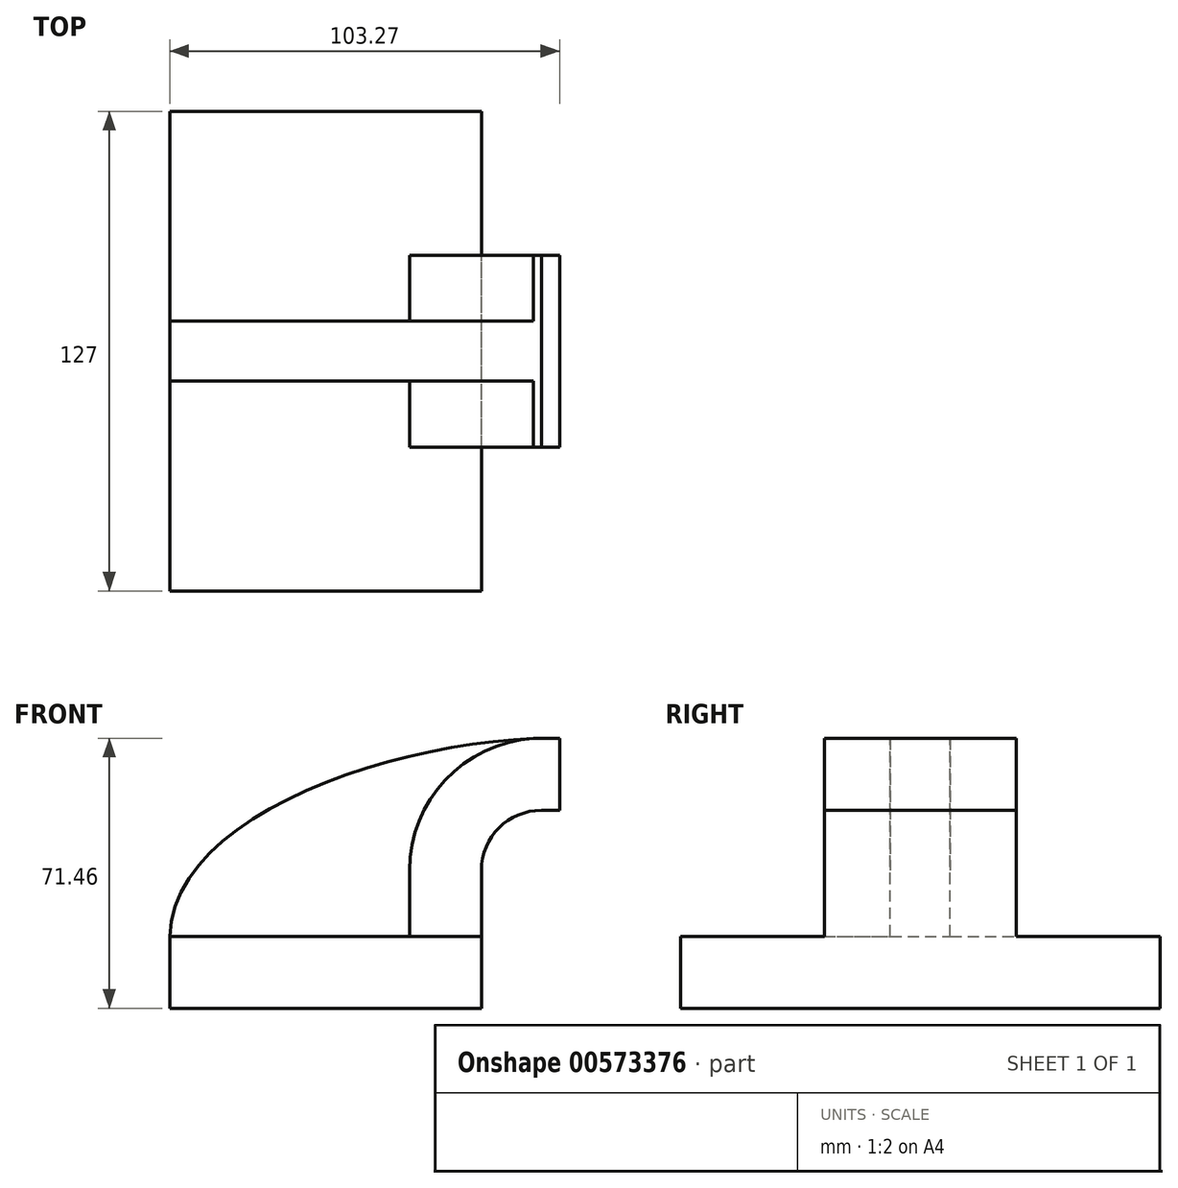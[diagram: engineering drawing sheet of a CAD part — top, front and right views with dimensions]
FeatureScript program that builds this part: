
annotation { "Feature Type Name" : "Feature", "Feature Type Description" : "" }
export const myFeature = defineFeature(function(context is Context, id is Id, definition is map)
    precondition{}
    {
        {
            var Q0;
            Q0=qCreatedBy(makeId("Front.planeOp"),FACE);
            var sketch = newSketch(context, id + "F0", { "sketchPlane" : qUnion([Q0])});
            skLineSegment(sketch, "E0.bottom", {"start": v(-41.28, -9.53) * mm, "end": v(41.28, -9.53) * mm});
            skLineSegment(sketch, "E0.top", {"start": v(-41.28, 9.53) * mm, "end": v(41.28, 9.53) * mm});
            skLineSegment(sketch, "E0.left", {"start": v(-41.28, -9.53) * mm, "end": v(-41.28, 9.53) * mm});
            skLineSegment(sketch, "E0.right", {"start": v(41.28, -9.53) * mm, "end": v(41.28, 9.53) * mm});
            skPoint(sketch, "E0.middle", {"position": v(0, 0) * mm});
            skLineSegment(sketch, "E1.bottom", {"start": v(109.46, 38.1) * mm, "end": v(62, 38.1) * mm});
            skLineSegment(sketch, "E1.top", {"start": v(109.46, 66.67) * mm, "end": v(62, 66.67) * mm});
            skLineSegment(sketch, "E1.left", {"start": v(109.46, 38.1) * mm, "end": v(109.46, 66.67) * mm});
            skLineSegment(sketch, "E1.right", {"start": v(62, 38.1) * mm, "end": v(62, 66.67) * mm});
            skPoint(sketch, "E1.middle", {"position": v(85.72, 52.39) * mm});
            skLineSegment(sketch, "E2", {"start": v(41.27, 9.53) * mm, "end": v(41.27, 27) * mm});
            skArc(sketch, "E3", {"start": v(41.27, 27) * mm, "mid": v(45.92, 38.23) * mm, "end": v(57.15, 42.88) * mm});
            skLineSegment(sketch, "E4", {"start": v(57.15, 42.88) * mm, "end": v(83.61, 42.88) * mm});
            skLineSegment(sketch, "E5.0", {"start": v(57.15, 61.93) * mm, "end": v(83.61, 61.93) * mm});
            skArc(sketch, "E5.1", {"start": v(22.23, 27) * mm, "mid": v(32.45, 51.7) * mm, "end": v(57.15, 61.93) * mm});
            skLineSegment(sketch, "E5.2", {"start": v(22.22, 9.53) * mm, "end": v(22.22, 27) * mm});
            skFitSpline(sketch, "E6", {"points": [v(-41.28, 9.53) * mm, v(57.15, 61.93) * mm], "startDerivative": vector(2.5, 96.11) * mm, "endDerivative": vector(118.65, 2.68) * mm});
            skLineSegment(sketch, "E7", {"start": v(83.61, 61.93) * mm, "end": v(83.61, 42.88) * mm});
            skSolve(sketch);
        }
        {
            var Q0;
            Q0=makeQuery(id+"F0.imprint","IMPRINT",FACE,{"disambiguationData":[TD([[makeQuery(id+"F0.imprint","IMPRINT",EDGE,{"derivedFrom":sQuery(id+"F0.wireOp",EDGE,"E0.bottom")}),1.0]])]});
            extrude(context, id + "F1", {"entities" : qUnion([Q0]), "endBound" : BoundingType.SYMMETRIC, "depth" : 127 * mm, "offsetDistance" : 25.4 * mm});
        }
        {
            var Q0;
            {var subQ0=sQuery(id+"F0.wireOp",EDGE,"E2");Q0=makeQuery(id+"F0.imprint","IMPRINT",FACE,{"disambiguationData":[TD([[makeQuery(id+"F0.imprint","IMPRINT",EDGE,{"derivedFrom":subQ0}),1.0]])]});}
            extrude(context, id + "F2", {"entities" : qUnion([Q0]), "operationType" : NewBodyOperationType.ADD, "endBound" : BoundingType.SYMMETRIC, "depth" : 50.8 * mm, "offsetDistance" : 25.4 * mm});
        }
        {
            var Q0;
            {var subQ3=sQuery(id+"F0.wireOp",EDGE,"E5.2");Q0=makeQuery(id+"F0.imprint","IMPRINT",FACE,{"disambiguationData":[TD([[makeQuery(id+"F0.imprint","IMPRINT",EDGE,{"derivedFrom":subQ3}),1.0]])]});}
            extrude(context, id + "F3", {"entities" : qUnion([Q0]), "operationType" : NewBodyOperationType.ADD, "endBound" : BoundingType.SYMMETRIC, "depth" : 15.88 * mm, "offsetDistance" : 25.4 * mm});
        }
    });
